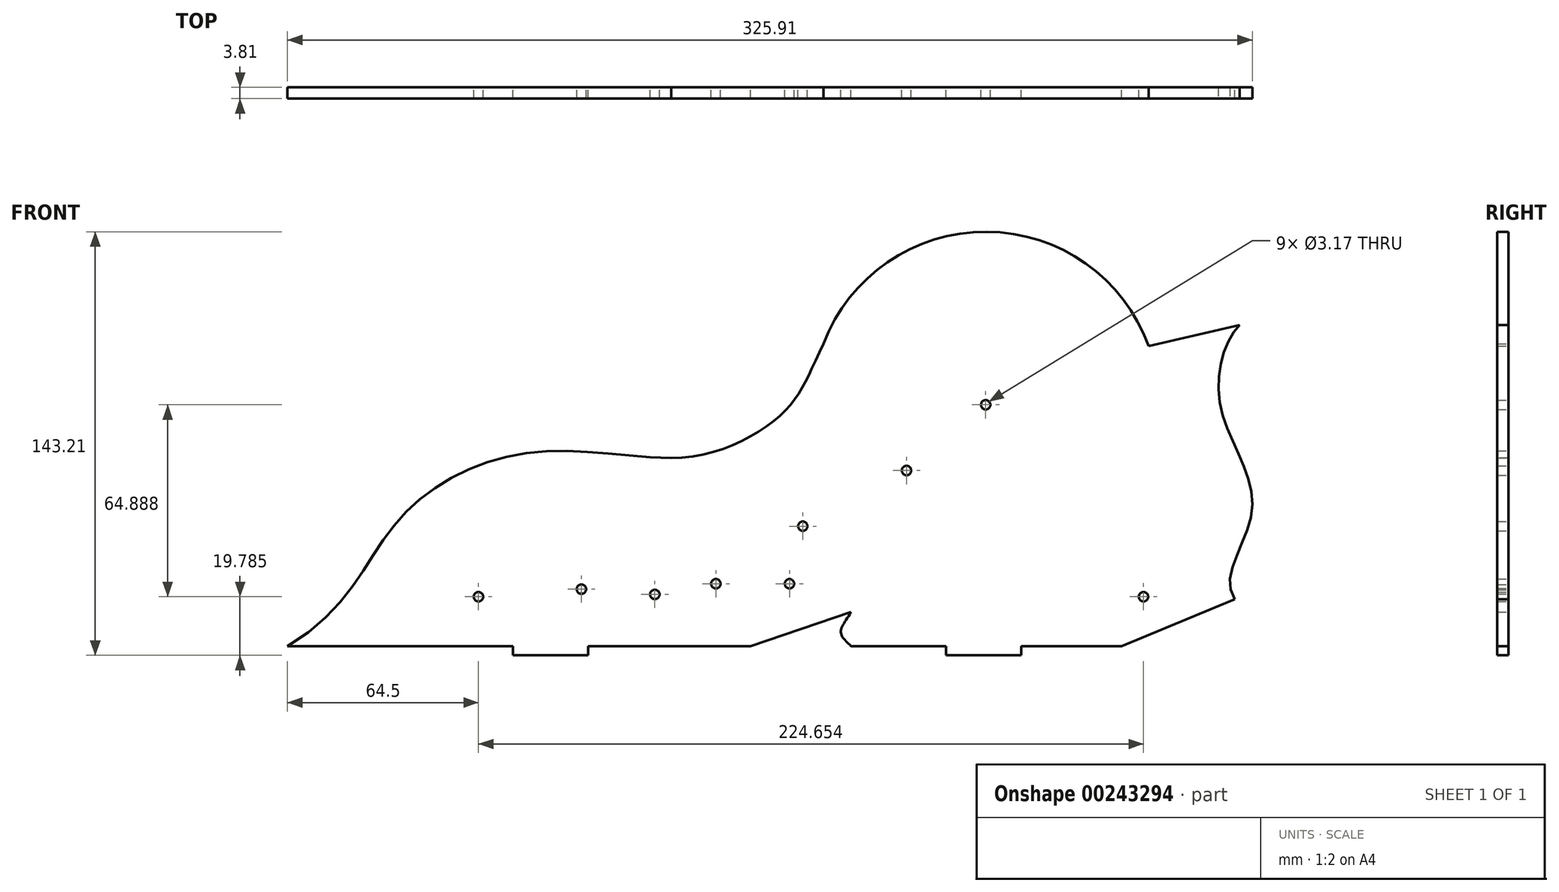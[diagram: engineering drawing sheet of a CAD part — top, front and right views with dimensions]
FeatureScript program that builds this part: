
annotation { "Feature Type Name" : "Feature", "Feature Type Description" : "" }
export const myFeature = defineFeature(function(context is Context, id is Id, definition is map)
    precondition{}
    {
        {
            var Q0;
            Q0=qCreatedBy(makeId("Front.planeOp"),FACE);
            var sketch = newSketch(context, id + "F0", { "sketchPlane" : qUnion([Q0])});
            skLineSegment(sketch, "E0.top", {"start": v(-43.1, 0) * mm, "end": v(11.74, 0) * mm});
            skCircle(sketch, "E1", {"center": v(29.36, 40.52) * mm, "radius": 1.59 * mm});
            skLineSegment(sketch, "E2", {"start": v(-144.7, 0) * mm, "end": v(-68.5, 0) * mm});
            skCircle(sketch, "E3", {"center": v(91.15, 81.55) * mm, "radius": 1.59 * mm});
            skCircle(sketch, "E4", {"center": v(64.4, 59.33) * mm, "radius": 1.59 * mm});
            skCircle(sketch, "E5", {"center": v(24.87, 21.07) * mm, "radius": 1.59 * mm});
            skCircle(sketch, "E6", {"center": v(0, 21.07) * mm, "radius": 1.59 * mm});
            skLineSegment(sketch, "E7", {"start": v(146.2, 101.45) * mm, "end": v(176.99, 108.58) * mm});
            skCircle(sketch, "E8", {"center": v(-20.61, 17.45) * mm, "radius": 1.59 * mm});
            skCircle(sketch, "E9", {"center": v(-45.42, 19.23) * mm, "radius": 1.59 * mm});
            skFitSpline(sketch, "E10", {"points": [v(42.71, 85.43) * mm, v(0, 64.34) * mm, v(-61.52, 65.57) * mm, v(-107.12, 42.69) * mm, v(-144.7, 0) * mm], "startDerivative": vector(-87.18, -109.32) * mm, "endDerivative": vector(-254.3, -148.83) * mm});
            skFitSpline(sketch, "E11", {"points": [v(176.99, 108.58) * mm, v(170.36, 81.6) * mm, v(181.09, 45.84) * mm, v(175.36, 15.8) * mm], "startDerivative": vector(-50.44, -50.2) * mm, "endDerivative": vector(52.78, -71.47) * mm});
            skLineSegment(sketch, "E12", {"start": v(175.36, 15.8) * mm, "end": v(137.1, 0) * mm});
            skLineSegment(sketch, "E13", {"start": v(45.62, 11.45) * mm, "end": v(11.74, 0) * mm});
            skFitSpline(sketch, "E14", {"points": [v(45.62, 11.45) * mm, v(42.23, 4.52) * mm, v(45.62, 0) * mm], "startDerivative": vector(-9.03, -15.75) * mm, "endDerivative": vector(9.75, -9.25) * mm});
            skLineSegment(sketch, "E15.trimOffspring", {"start": v(45.62, 0) * mm, "end": v(77.74, 0) * mm});
            skCircle(sketch, "E16", {"center": v(-80.19, 16.66) * mm, "radius": 1.59 * mm});
            skCircle(sketch, "E17", {"center": v(144.46, 16.66) * mm, "radius": 1.59 * mm});
            skArc(sketch, "E18", {"start": v(146.2, 101.45) * mm, "mid": v(91.53, 140.08) * mm, "end": v(36.37, 102.16) * mm});
            skPoint(sketch, "E19.startDerivative.orphan", {"position": v(5.5, 72.9) * mm});
            skPoint(sketch, "E20.1.internal.orphan", {"position": v(25.94, 72.9) * mm});
            skFitSpline(sketch, "E21", {"points": [v(-15.08, 63.52) * mm, v(23.06, 79.26) * mm, v(36.37, 102.16) * mm], "startDerivative": vector(83.27, -0.1) * mm, "endDerivative": vector(35.25, 70.94) * mm});
            skLineSegment(sketch, "E22.top", {"start": v(-68.5, -3.12) * mm, "end": v(-43.1, -3.12) * mm});
            skLineSegment(sketch, "E22.left", {"start": v(-68.5, 0) * mm, "end": v(-68.5, -3.12) * mm});
            skLineSegment(sketch, "E22.right", {"start": v(-43.1, 0) * mm, "end": v(-43.1, -3.12) * mm});
            skLineSegment(sketch, "E23.top", {"start": v(77.74, -3.12) * mm, "end": v(103.14, -3.12) * mm});
            skLineSegment(sketch, "E23.left", {"start": v(77.74, 0) * mm, "end": v(77.74, -3.12) * mm});
            skLineSegment(sketch, "E23.right", {"start": v(103.14, 0) * mm, "end": v(103.14, -3.12) * mm});
            skLineSegment(sketch, "E24.trimOffspring", {"start": v(103.14, 0) * mm, "end": v(137.1, 0) * mm});
            skSolve(sketch);
        }
        {
            var Q0;
            Q0 = qSketchRegion(id + "F0", true);
            extrude(context, id + "F1", {"entities" : qUnion([Q0]), "depth" : 3.8 * mm});
        }
    });
